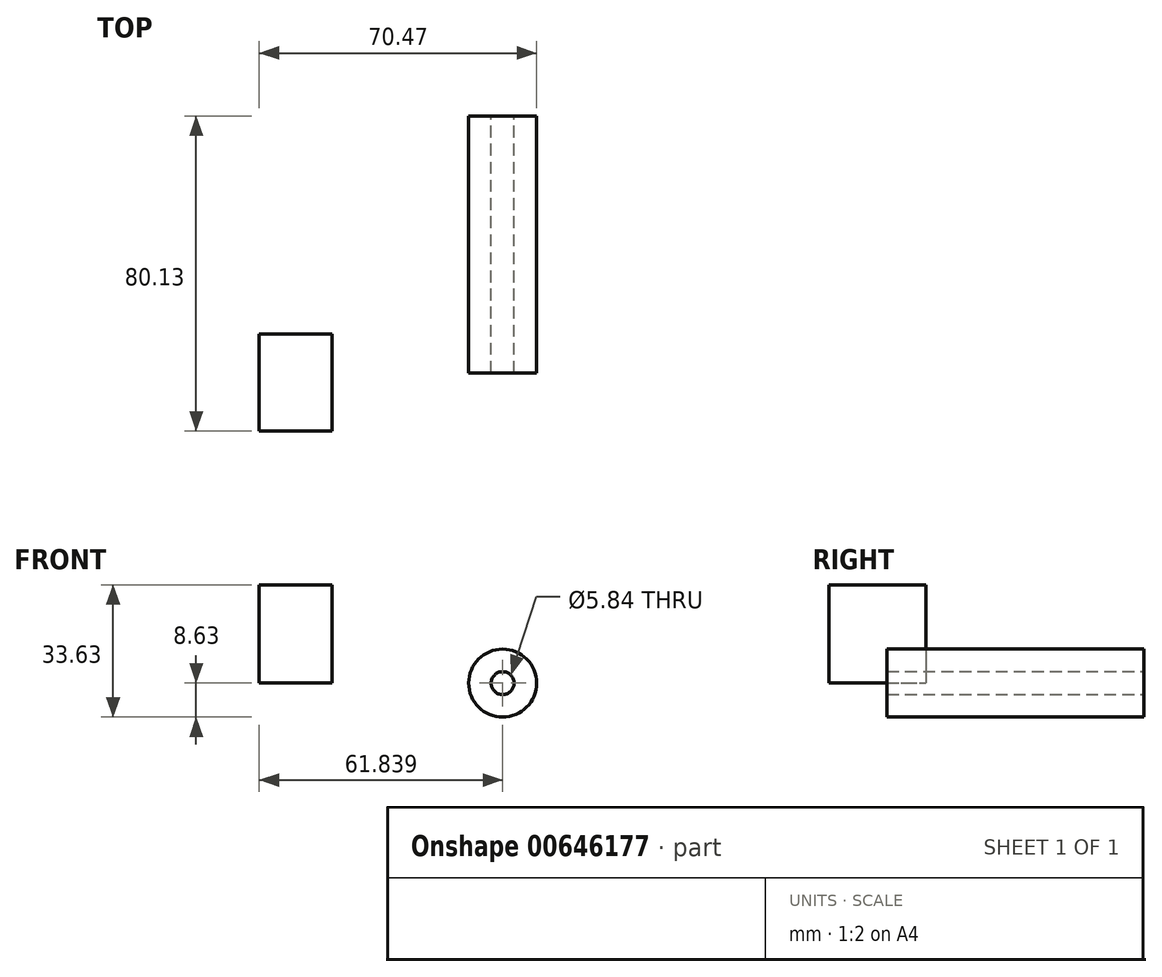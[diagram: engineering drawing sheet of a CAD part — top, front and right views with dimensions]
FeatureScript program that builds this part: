
annotation { "Feature Type Name" : "Feature", "Feature Type Description" : "" }
export const myFeature = defineFeature(function(context is Context, id is Id, definition is map)
    precondition{}
    {
        {
            var Q0;
            Q0=qCreatedBy(makeId("Top.planeOp"),FACE);
            var sketch = newSketch(context, id + "F0", { "sketchPlane" : qUnion([Q0])});
            skLineSegment(sketch, "E0.bottom", {"start": v(-58.92, -49.7) * mm, "end": v(-40.46, -49.7) * mm});
            skLineSegment(sketch, "E0.top", {"start": v(-58.92, -25.03) * mm, "end": v(-40.46, -25.03) * mm});
            skLineSegment(sketch, "E0.left", {"start": v(-58.92, -49.7) * mm, "end": v(-58.92, -25.03) * mm});
            skLineSegment(sketch, "E0.right", {"start": v(-40.46, -49.7) * mm, "end": v(-40.46, -25.03) * mm});
            skSolve(sketch);
        }
        {
            var Q0;
            Q0=makeQuery(id+"F0.imprint","IMPRINT",FACE,{"disambiguationData":[TD([[makeQuery(id+"F0.imprint","IMPRINT",EDGE,{"derivedFrom":sQuery(id+"F0.wireOp",EDGE,"E0.bottom")}),1.0]])]});
            extrude(context, id + "F1", {"entities" : qUnion([Q0]), "depth" : 25 * mm, "offsetDistance" : 25 * mm});
        }
        {
            var Q0;
            Q0=qCreatedBy(makeId("Top.planeOp"),FACE);
            var sketch = newSketch(context, id + "F2", { "sketchPlane" : qUnion([Q0])});
            skLineSegment(sketch, "E1.bottom", {"start": v(0, -34.89) * mm, "end": v(-5.71, -34.89) * mm});
            skLineSegment(sketch, "E1.top", {"start": v(0, 30.42) * mm, "end": v(-5.71, 30.42) * mm});
            skLineSegment(sketch, "E1.left", {"start": v(0, -34.89) * mm, "end": v(0, 30.42) * mm});
            skLineSegment(sketch, "E1.right", {"start": v(-5.71, -34.89) * mm, "end": v(-5.71, 30.42) * mm});
            skLineSegment(sketch, "E2", {"start": v(2.92, 30.29) * mm, "end": v(2.92, -35.1) * mm});
            skSolve(sketch);
        }
        {
            var Q0;
            Q0=makeQuery(id+"F2.imprint","IMPRINT",FACE,{"disambiguationData":[TD([[makeQuery(id+"F2.imprint","IMPRINT",EDGE,{"derivedFrom":sQuery(id+"F2.wireOp",EDGE,"E1.bottom")}),-1.0]])]});
            var Q1;
            Q1=sQuery(id+"F2.wireOp",EDGE,"E2");
            revolve(context, id + "F3", {"entities" : qUnion([Q0]), "axis" : qUnion([Q1]), "revolveType" : RevolveType.FULL});
        }
    });
